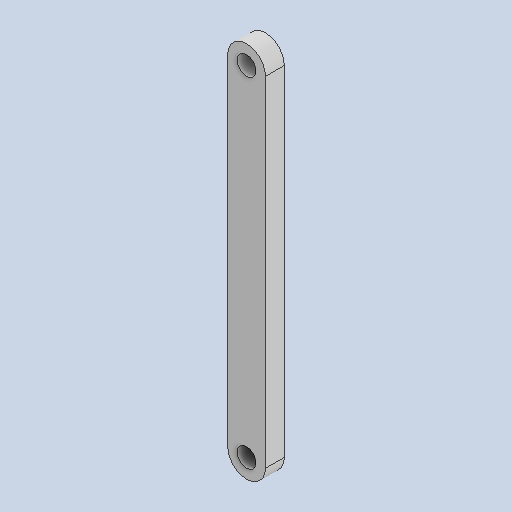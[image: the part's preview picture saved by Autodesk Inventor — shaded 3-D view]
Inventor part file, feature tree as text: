
AUTODESK INVENTOR PART (.ipt)
format: ipt  version: 2024.3 (Build 283343000, 343)  size: 251,392 bytes
history: native  units: mm
features: other x1, extrude x1, sketch x1
ambient origin geometry x8: Origin, YZ Plane, XZ Plane, XY Plane, X Axis, Y Axis, Z Axis, Center Point
bodies: Body1 (feature_tree)
feature tree (3):
  other  "ソリッド1"
  extrude  "押し出し1"  Depth=10.0mm
  sketch  "スケッチ1"
